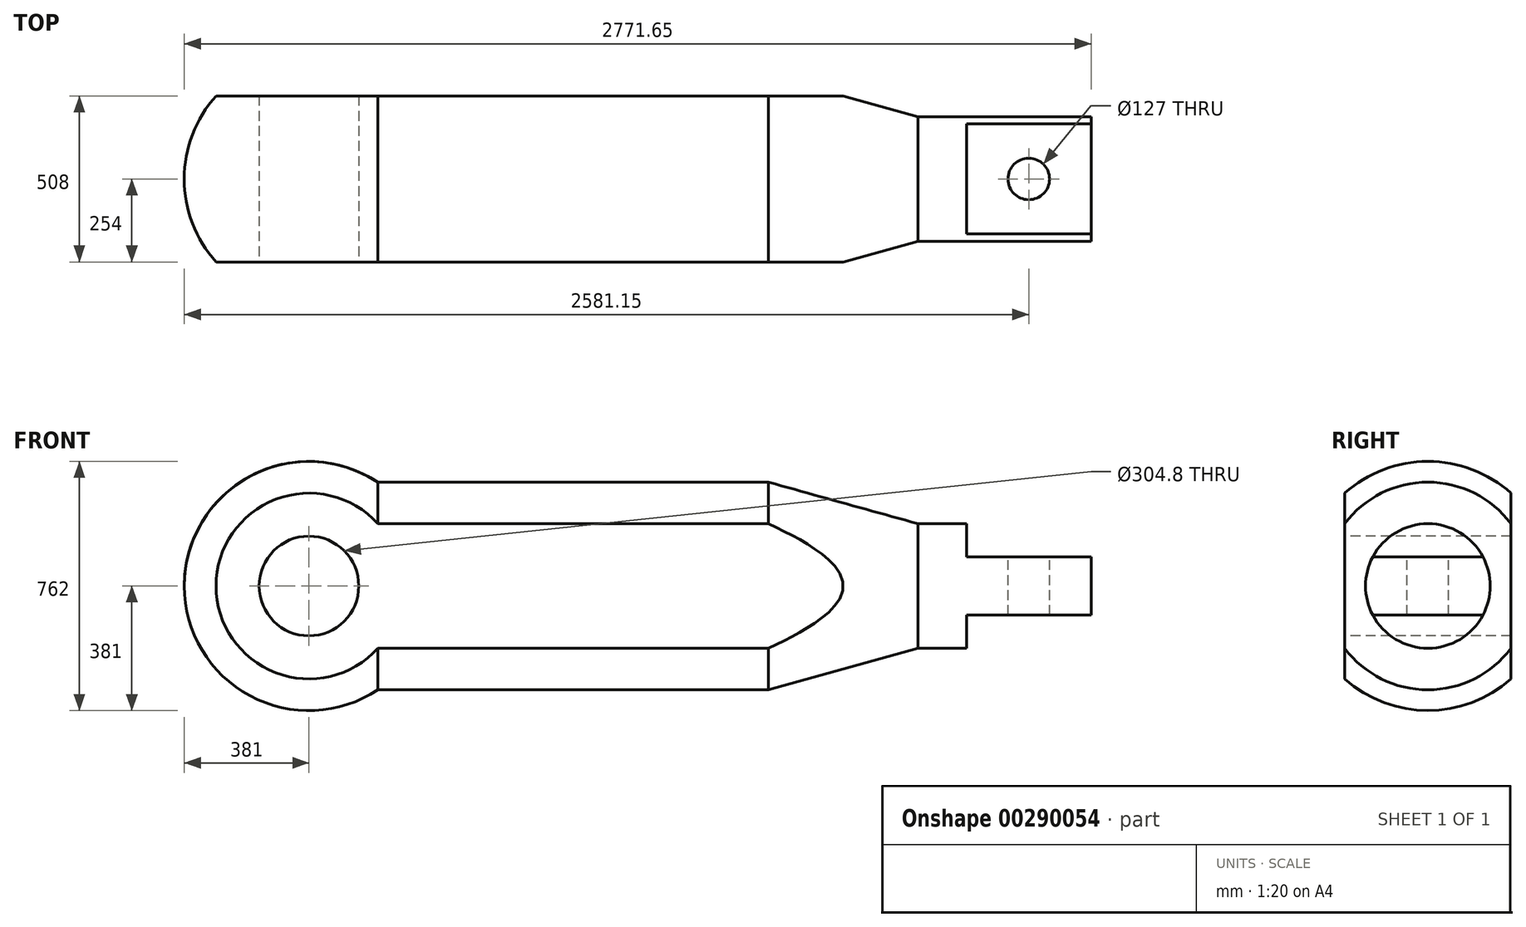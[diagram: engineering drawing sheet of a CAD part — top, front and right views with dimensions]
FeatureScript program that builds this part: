
annotation { "Feature Type Name" : "Feature", "Feature Type Description" : "" }
export const myFeature = defineFeature(function(context is Context, id is Id, definition is map)
    precondition{}
    {
        {
            var Q0;
            Q0=qCreatedBy(makeId("Front.planeOp"),FACE);
            var sketch = newSketch(context, id + "F0", { "sketchPlane" : qUnion([Q0])});
            skLineSegment(sketch, "E0", {"start": v(0, 0) * mm, "end": v(1739.9, 0) * mm, "construction": true});
            skArc(sketch, "E1", {"start": v(-381, 0) * mm, "mid": v(-180.17, 335.7) * mm, "end": v(210.6, 317.5) * mm});
            skLineSegment(sketch, "E2", {"start": v(210.6, 317.5) * mm, "end": v(1404.4, 317.5) * mm});
            skLineSegment(sketch, "E3", {"start": v(1404.4, 317.5) * mm, "end": v(1861.6, 190.5) * mm});
            skLineSegment(sketch, "E4", {"start": v(1861.6, 190.5) * mm, "end": v(2390.65, 190.5) * mm});
            skLineSegment(sketch, "E5", {"start": v(2390.65, 190.5) * mm, "end": v(2390.65, 0) * mm});
            skLineSegment(sketch, "E6", {"start": v(1644.67, 0) * mm, "end": v(1709.2, 0) * mm});
            skLineSegment(sketch, "E7", {"start": v(2390.65, 0) * mm, "end": v(-381, 0) * mm});
            skLineSegment(sketch, "E8", {"start": v(0, 0) * mm, "end": v(3059.95, 0) * mm, "construction": true});
            skSolve(sketch);
        }
        {
            var Q0;
            Q0 = qSketchRegion(id + "F0", true);
            var Q1;
            Q1=sQuery(id+"F0.wireOp",EDGE,"E8");
            revolve(context, id + "F1", {"entities" : qUnion([Q0]), "axis" : qUnion([Q1]), "revolveType" : RevolveType.FULL});
        }
        {
            var Q0;
            Q0=qCreatedBy(makeId("Front.planeOp"),FACE);
            var sketch = newSketch(context, id + "F2", { "sketchPlane" : qUnion([Q0])});
            skLineSegment(sketch, "E9.bottom", {"start": v(2390.65, 191.1) * mm, "end": v(2009.65, 191.1) * mm});
            skLineSegment(sketch, "E9.top", {"start": v(2390.65, 88.9) * mm, "end": v(2009.65, 88.9) * mm});
            skLineSegment(sketch, "E9.left", {"start": v(2390.65, 191.1) * mm, "end": v(2390.65, 88.9) * mm});
            skLineSegment(sketch, "E9.right", {"start": v(2009.65, 191.1) * mm, "end": v(2009.65, 88.9) * mm});
            skLineSegment(sketch, "E10", {"start": v(1624.3, 0) * mm, "end": v(2989.97, 0) * mm, "construction": true});
            skLineSegment(sketch, "E11.MirrorCS", {"start": v(2390.65, -191.1) * mm, "end": v(2390.65, -88.9) * mm});
            skLineSegment(sketch, "E12.MirrorCS", {"start": v(2009.65, -191.1) * mm, "end": v(2009.65, -88.9) * mm});
            skLineSegment(sketch, "E13.MirrorCS", {"start": v(2390.65, -88.9) * mm, "end": v(2009.65, -88.9) * mm});
            skLineSegment(sketch, "E14.MirrorCS", {"start": v(2390.65, -191.1) * mm, "end": v(2009.65, -191.1) * mm});
            skSolve(sketch);
        }
        {
            var Q0;
            Q0 = qSketchRegion(id + "F2", true);
            extrude(context, id + "F3", {"entities" : qUnion([Q0]), "operationType" : NewBodyOperationType.REMOVE, "endBound" : BoundingType.THROUGH_ALL, "oppositeDirection" : true, "depth" : 25.4 * mm, "hasSecondDirection" : true, "secondDirectionBound" : SecondDirectionBoundingType.THROUGH_ALL, "secondDirectionOppositeDirection" : false, "secondDirectionDepth" : 25.4 * mm});
        }
        {
            var Q0;
            Q0=makeQuery(id+"F1.opRevolve","SWEPT_FACE",FACE,{"disambiguationData":[OSD([sQuery(id+"F0.wireOp",EDGE,"E5")])]});
            var sketch = newSketch(context, id + "F4", { "sketchPlane" : qUnion([Q0])});
            skLineSegment(sketch, "E15", {"start": v(-254, 391.35) * mm, "end": v(-254, -387.04) * mm});
            skCircle(sketch, "E16", {"center": v(0, 0) * mm, "radius": 381 * mm});
            skLineSegment(sketch, "E17", {"start": v(254, 397.83) * mm, "end": v(254, -392.07) * mm});
            skLineSegment(sketch, "E18", {"start": v(0, 0) * mm, "end": v(0, 394.95) * mm, "construction": true});
            skSolve(sketch);
        }
        {
            var Q0;
            {var subQ0=sQuery(id+"F4.wireOp",EDGE,"E16");var subQ1=sQuery(id+"F4.wireOp",EDGE,"E15");var subQ2=makeQuery(id+"F4.imprint","INTERSECT",VERTEX,{"disambiguationData":[OD(0.0)],"derivedFrom":[subQ1,subQ0]});Q0=makeQuery(id+"F4.imprint","IMPRINT",FACE,{"disambiguationData":[TD([[makeQuery(id+"F4.imprint","IMPRINT",EDGE,{"disambiguationData":[TD([[subQ2,-1.0]])],"derivedFrom":subQ1}),-1.0]])]});}
            var Q1;
            {var subQ0=sQuery(id+"F4.wireOp",EDGE,"E17");var subQ1=sQuery(id+"F4.wireOp",EDGE,"E16");var subQ2=makeQuery(id+"F4.imprint","INTERSECT",VERTEX,{"disambiguationData":[OD(0.0)],"derivedFrom":[subQ1,subQ0]});Q1=makeQuery(id+"F4.imprint","IMPRINT",FACE,{"disambiguationData":[TD([[makeQuery(id+"F4.imprint","IMPRINT",EDGE,{"disambiguationData":[TD([[subQ2,1.0]])],"derivedFrom":subQ1}),1.0]])]});}
            extrude(context, id + "F5", {"entities" : qUnion([Q0, Q1]), "operationType" : NewBodyOperationType.REMOVE, "endBound" : BoundingType.THROUGH_ALL, "oppositeDirection" : true, "depth" : 25.4 * mm});
        }
        {
            var Q0;
            Q0=makeQuery(id+"F5.boolean.opBoolean","COPY",FACE,{"derivedFrom":makeQuery(id+"F5.opExtrude","SWEPT_FACE",FACE,{"disambiguationData":[OSD([sQuery(id+"F4.wireOp",EDGE,"E15")])]})});
            var sketch = newSketch(context, id + "F6", { "sketchPlane" : qUnion([Q0])});
            skCircle(sketch, "E19", {"center": v(0, 0) * mm, "radius": 152.4 * mm});
            skSolve(sketch);
        }
        {
            var Q0;
            Q0 = qSketchRegion(id + "F6", true);
            extrude(context, id + "F7", {"entities" : qUnion([Q0]), "operationType" : NewBodyOperationType.REMOVE, "endBound" : BoundingType.THROUGH_ALL, "oppositeDirection" : true, "depth" : 25.4 * mm});
        }
        {
            var Q0;
            Q0=makeQuery(id+"F3.boolean.opBoolean","COPY",FACE,{"derivedFrom":makeQuery(id+"F3.opExtrude","SWEPT_FACE",FACE,{"disambiguationData":[OSD([sQuery(id+"F2.wireOp",EDGE,"E9.top")])]})});
            var sketch = newSketch(context, id + "F8", { "sketchPlane" : qUnion([Q0])});
            skCircle(sketch, "E20", {"center": v(2200.15, 0) * mm, "radius": 63.5 * mm});
            skSolve(sketch);
        }
        {
            var Q0;
            Q0 = qSketchRegion(id + "F8", true);
            extrude(context, id + "F9", {"entities" : qUnion([Q0]), "operationType" : NewBodyOperationType.REMOVE, "endBound" : BoundingType.THROUGH_ALL, "oppositeDirection" : true, "depth" : 25.4 * mm});
        }
    });
